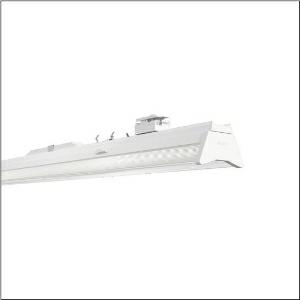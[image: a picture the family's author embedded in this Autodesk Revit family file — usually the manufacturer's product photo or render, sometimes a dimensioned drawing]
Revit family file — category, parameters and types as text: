
# Revit family: licross_21_performance_ho_52tm16dn4e5m
name_source: partatom
category: Lighting Fixtures
units: mm (PartAtom-declared; Revit-internal decimal feet)

## family parameters
Cut with Voids When Loaded = No
Host = Face
Light Source = No
Part Type = Normal
Room Calculation Point = No
Round Connector Dimension = Use Diameter
Shared = No

## types (1)
- --- (1 x LED, 14870 lm, 84.9 W, 4000K)
    Apparent Load = 85 VA
    CIE Flux Codes = 63 87 95 78 100
    Color Rendering = 80
    Color Temperature = 4000K
    Default Elevation = 1800 mm
    Description = Licross 21 Performance HO, luminaire insert, of sheet steel, galvanised, coil coated, white, length: 1.500mm, width: 120mm, height: 123mm, LED rated luminous flux: 14.870lm, light colour: 840, SDCM (Standard Deviation of Colour Matching)MacAdam ≤ 3 SDCM (initial), control gear: DALI 2, with plug, 5-pole, with phase selection, mains connection: 220..240V, AC, 50/60Hz, rated input power: 85W, internal wiring halogen-free, primary light control with lens, of plastic, primary optical cover: cover, of PMMA, light emission: direct/indirect distribution, primary light characteristic: symmetric, protection rating (complete): IP40, insulation class (complete): insulation class I (protective earthing), certification: CE, ENEC, UKCA, protection symbol: D if used in an environment without relevant dust loads with corresponding accessories, impact resistance: IK06, permissible ambient temperature for indoor applications: -25..+35°C, corresponds to IFS (International Featured Standards) requirements for safety and quality in the food industry, reducing of maximum allowable ambient temperature of 5°C with ceiling mounting, LABS conformity tested according to VDMA 24364:2018-05, The light source and the operating device comply with the requirements of the Ecodesign Regulation (EU) 2019/2020 and are replaceable in accordance with this regulation, packaging unit: 1 piece
    Height = 114 mm
    Lamp = 1 x LED
    Lamp Light Flux = 14870 lm
    Lamp Power = 84.9 W
    Lamp count = 1
    Length = 1500 mm
    Luminous efficacy = 175 lm/W
    Manufacturer = Siteco
    ModVariant = No
    Model = 52TM16DN4E5M
    Mounting Place = Ceiling
    Mounting Type = Pendant
    Number of Poles = 1
    OnlyDefault = Yes
    Power Factor = 1
    Product Name = Licross 21 Performance HO
    Product group = luminaire insert | ceiling pendant
    ProductGroupID = 901
    Protection Class = Protection class I
    Protection Degree = IP 40
    RLX_Detail_Level = 1
    RLX_Emergency_Light_Flux = 0 lm
    RLX_Emergency_Type = 0
    RLX_Emergency_Type_DB = No
    RlxData = <blob elided: 34361 chars, md5=0ea15dd5>
    Socket = socket
    Standby Power = 0 W
    System Light Flux = 14870 lm
    System Power = 85 W
    Type Comments = factory setting: luminous flux: 100 % | dim-lin: 254 | 484 mA
    Type Image = l_1256138.jpg
    URL = http://relux.com
    VarID = @adj_129515
    Voltage = 0 V
    Weight = 0.00 kg
    Width = 120 mm

## geometry (parser evidence)
native form markers: Blend x4, Sweep x11
no freeform markers — native parametric forms only
